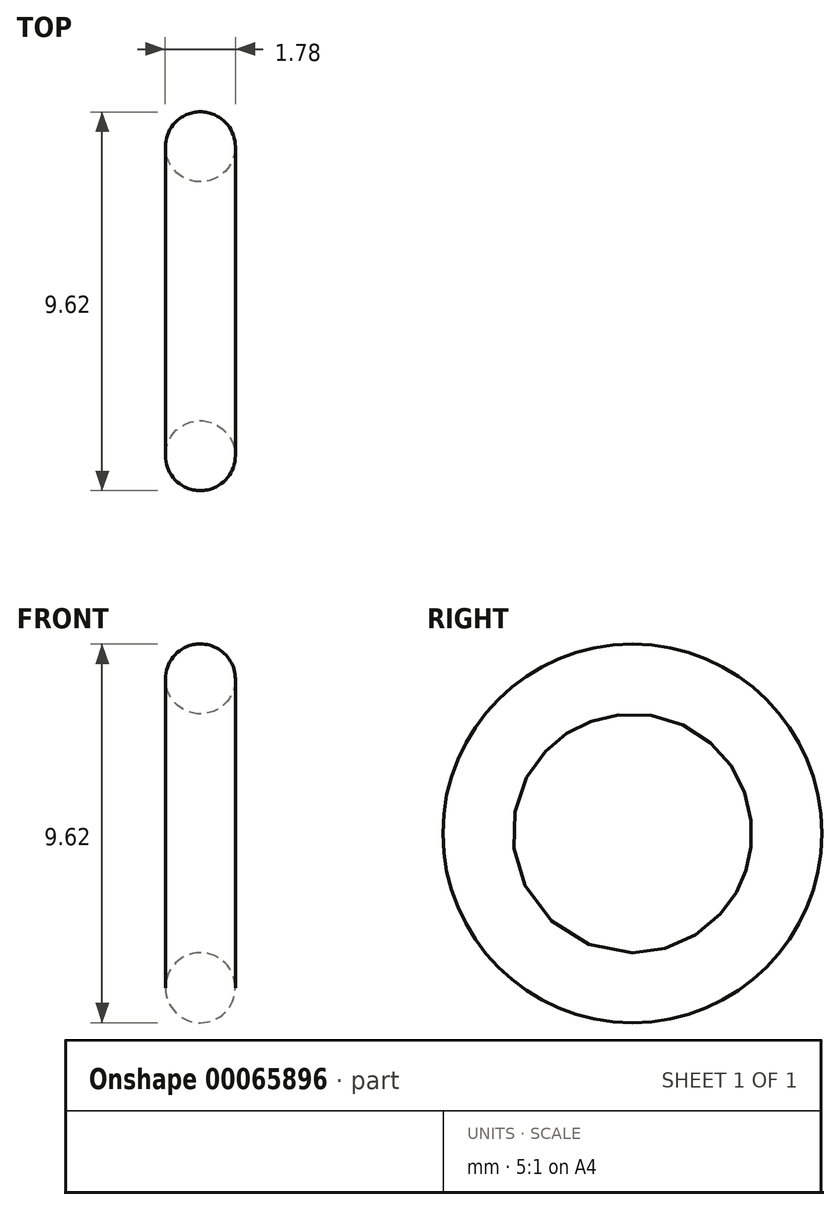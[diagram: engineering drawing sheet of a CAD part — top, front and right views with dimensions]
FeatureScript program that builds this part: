
annotation { "Feature Type Name" : "Feature", "Feature Type Description" : "" }
export const myFeature = defineFeature(function(context is Context, id is Id, definition is map)
    precondition{}
    {
        {
            var Q0;
            Q0=qCreatedBy(makeId("Front.planeOp"),FACE);
            var sketch = newSketch(context, id + "F0", { "sketchPlane" : qUnion([Q0])});
            skLineSegment(sketch, "E0", {"start": v(0, 0) * mm, "end": v(-6.06, 0) * mm, "construction": true});
            skCircle(sketch, "E1", {"center": v(0, 3.92) * mm, "radius": 0.89 * mm});
            skSolve(sketch);
        }
        {
            var Q0;
            Q0=makeQuery(id+"F0.imprint","IMPRINT",FACE,{"disambiguationData":[TD([[makeQuery(id+"F0.imprint","IMPRINT",EDGE,{"derivedFrom":sQuery(id+"F0.wireOp",EDGE,"E1")}),1.0]])]});
            var Q1;
            Q1=sQuery(id+"F0.wireOp",EDGE,"E0");
            revolve(context, id + "F1", {"entities" : qUnion([Q0]), "axis" : qUnion([Q1]), "revolveType" : RevolveType.FULL});
        }
    });
